# Revit family: SIMES_B.9000W_BRICK LIGHT
name_source: partatom
category: Lighting Fixtures
revit_build: Autodesk Revit 2016 (Build: 20150714_1515(x64)
units: mm (PartAtom-declared; Revit-internal decimal feet)

## family parameters
Cut with Voids When Loaded = No
Host = Face
Light Source = Yes
OmniClass Number = 23.80.70.14
OmniClass Title = Luminaries for External Lighting
Part Type = Normal
Room Calculation Point = No
Round Connector Dimension = Use Diameter
Shared = No

## types (1)
- SIMES_B.9000W_BRICK LIGHT
    Approval mark = CE
    BIMobject category = Outside
    BIMobject category code = lighting-outside
    BIMobject main category = Lighting
    BIMobject main category code = lighting
    Brand url = http://www.simes.it
    Color Filter = 16777215
    Color Rendering Index = CRI 80
    Colour Temperature = 3000
    Default Elevation = 1219 mm
    Description = BRICK LIGHT WALL RECESSED
Art. B.9000W
MODULES LED 3000K  24V CRI 80
Rated luminaire luminous flux: 120lm
Rated input power: 2.5W
Luminaire efficacy: 48lm/W
Without trasformer
CE

PRODUCT TYPE
Wall recessed luminaire (version B.9000W). Surface mounted luminaire (version B.9005W). IP rating IP 65
MATERIAL CHARACTERISTICS
Base in aluminium die cast housing in EN AB-47100 (low copper content) with high resistance against corrosion. Stone wash surface treatment prior to painting process. A4 grade Stainless Steel screws with 2,5-3% molybdenum content which increases the resistance against corrosion. Diffuser made of acid-etched pressed glass. Painting Process : 3 Step Process
1) Surface treatment with BONDERITE. A heavy metal free chemical surface treatment containing ceramic nano particles giving a cohesive, inorganic and highly dense protective coating. 2) PRE POLYMERIZATION a process of introducing an epoxy primer with excellent characteristics to the paint which also offers very high resistance to oxidation due to its Zinc content. 3) POLYMERIZATION a process with the application of polyester powder with high resistance against UV rays and harsh weather conditions. Resistance test protection for Marine applications for 1200h.  Mechanical resistance IK 08. Compression resistance: Full brick 60N/mm², BRICK LIGHT 100N/mm².
LIGHTING PERFORMANCE
LOR -- 
INSTALLATION AND MAINTENANCE
This product has been manufactured with hand crafted procedures, therefore small imperfections, subsidence of the glass surface, actual cracks and future, colour ripples and variations over time, are deliberately present and they are a feature of the glass, proving the hand-made manufacturing procedure.
WIRING
Luminaire hard wired with 5m single neoprene cable for installation in exposed brick walls or other construction materials in place  (version B.9000W). Luminaire operating on Lithium polymers fed Battery via a micro USB plug with a maximum power of 8 hours to be used as a portable decorative luminaire for the exterior.
ON-OFF switch concealed at the bottom of the base and lateral three step (30% - 70%- 100%) dimming switch. Supplied with Micro USB cable. Power supply 230V available on request  (version B.9005W). Isolation: CLASS III . Available colours: White (cod.01). Weight: 3 Kg Glow Wire test: --
Lamp included.
BRICK LIGHT PATENT PENDING, REGISTERED DESIGN
Brick Light has been developed with reference to the standard Italian brick.
This luminaire contains built-in LED modules with energy class: A, A+, A++. In case of damage or malfunction please contact the manufacturer to receive additional instructions on how to replace and relative spare parts to order. The LED modules cannot be handled in the luminaire by the end user (Regulation UE 874/2012).
LED circuit boards are engineered accordingly to actual Lumen Maintenance regulation (LM80) and Technical Memorandum (TM21) where uniformity and quality of light is 50.000 hours referred to L70  B20 Ta 25°C.Lifecycle refers to LED circuit boards only, all others components of the luminaire are excluded.
    Design country = Italy
    Dimming Lamp Color Temperature Shift = <None>
    Edition number = 1
    Frequency = 0Hz
    IFC Classification = Light Fixture
    IK Rating = IK 08
    Lamp = 1 LED
    Lamp Light Flux = 300
    Lamp count = 1
    Last Update = 21/08/2017 10:06:27
    Lifetime = 50000 L70 B20 Ta 25°C
    Light Output Ratio = 100
    Light Source Symbol Size = 610 mm
    Luminous efficacy = 48
    Manufacturer = SIMES
    Manufacturer country = Italy
    Manufacturer name = Simes
    Masterformat 2014 Code = 26 56 00
    Masterformat 2014 Description = Exterior Lighting
    Material main = Glass
    Material secondary = Aluminium
    Model = B.9000W
    Mounting Place = Wall
    Mounting Type = Surface mounted
    NBS Reference Code = 49
    NBS Reference Description = Luminaires And Lamps
    Nominal height = 120 mm
    Nominal width = 250 mm  [stored 0.82021 ft]
    OmniClass Code = 23-35 47 11
    OmniClass Description = Lighting Fixtures
    Product Guid = ef36f838-f1ae-4f97-87ec-5203fcc9ee8a
    Product SKU = BRICK-LIGHT
    Product certification = http://www.simes.it
    Product data url = https://bimobject.com
    Product family = Wall recessed
    Product group = BRICK LIGHT
    Product url = http://www.simes.it
    Protection Class = Protection class III
    Protection Degree = IP 65
    QR code = http://bimobject.com
    System Light Flux = 120
    System Power = 2.5
    Technical description = http://www.simes.it
    Type Comments = SIMES S.p.A. - All rights reserved
    Type Image = bricklight-wallrecessed.jpg
    UNSPSC Code = 3911
    URL = https://www.simes.it
    Uniclass 1.4 Code = JY73
    Uniclass 1.4 Description = Luminaires and lamps
    Uniclass 2.0 Code = PR-49
    Uniclass 2.0 Description = Luminaires And Lamps
    Uniclass 2015 Code = EF_70_80
    Uniclass 2015 Name = Lighting
    Uniformat II Code = D5020
    Uniformat II Description = Lighting & Branch Wiring
    Voltage = 24V
    Weight Net (Kg) = 3
    Youtube clip = https://vimeo.com

note: [stored X ft] marks values corroborated as IEEE doubles in the binary element streams (Revit-internal decimal feet)

## geometry (parser evidence)
native form markers: Blend x4, Sweep x1
no freeform markers — native parametric forms only
